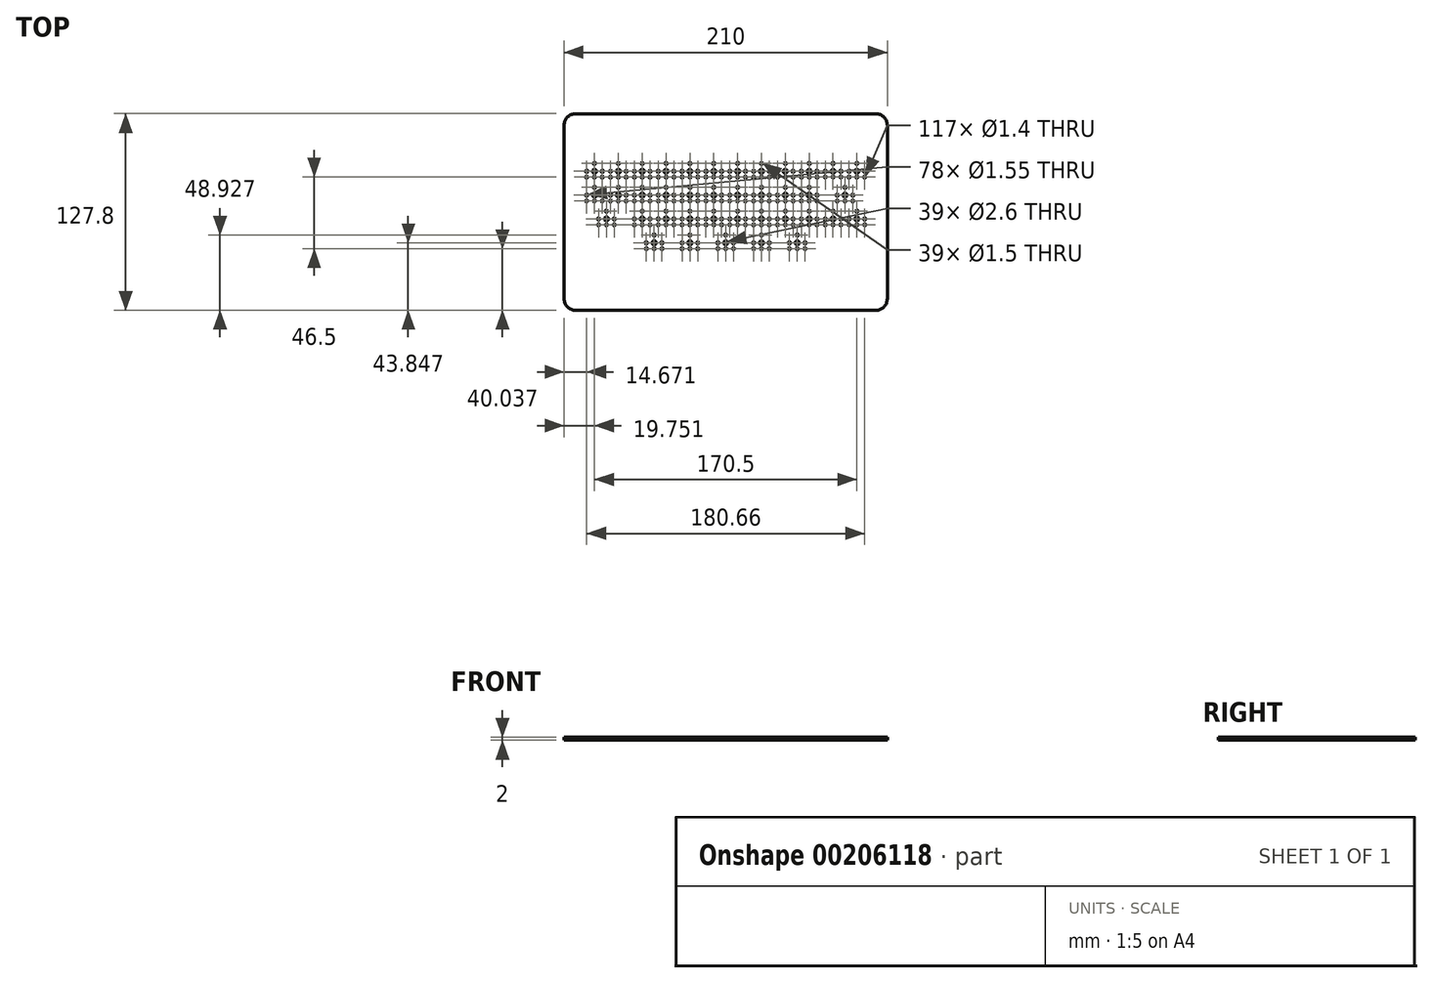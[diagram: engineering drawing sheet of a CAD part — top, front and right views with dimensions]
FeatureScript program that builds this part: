
annotation { "Feature Type Name" : "Feature", "Feature Type Description" : "" }
export const myFeature = defineFeature(function(context is Context, id is Id, definition is map)
    precondition{}
    {
        {
            var Q0;
            Q0=qCreatedBy(makeId("Top.planeOp"),FACE);
            var sketch = newSketch(context, id + "F0", { "sketchPlane" : qUnion([Q0])});
            skLineSegment(sketch, "E0", {"start": v(-79.74, 27.29) * mm, "end": v(-79.74, 14.29) * mm, "construction": true});
            skLineSegment(sketch, "E1.bottom", {"start": v(-73.74, 26.49) * mm, "end": v(-85.74, 26.49) * mm, "construction": true});
            skLineSegment(sketch, "E1.top", {"start": v(-73.74, 15.09) * mm, "end": v(-85.74, 15.09) * mm, "construction": true});
            skLineSegment(sketch, "E1.left", {"start": v(-73.74, 26.49) * mm, "end": v(-73.74, 15.09) * mm, "construction": true});
            skLineSegment(sketch, "E1.right", {"start": v(-85.74, 26.49) * mm, "end": v(-85.74, 15.09) * mm, "construction": true});
            skPoint(sketch, "E1.middle", {"position": v(-79.74, 20.79) * mm});
            skLineSegment(sketch, "E2", {"start": v(-79.74, 15.09) * mm, "end": v(-79.74, 20.09) * mm, "construction": true});
            skCircle(sketch, "E3", {"center": v(-79.74, 20.09) * mm, "radius": 1.3 * mm});
            skLineSegment(sketch, "E4", {"start": v(-79.74, 20.09) * mm, "end": v(-79.74, 17.59) * mm, "construction": true});
            skLineSegment(sketch, "E5", {"start": v(-79.74, 20.09) * mm, "end": v(-79.74, 16.28) * mm, "construction": true});
            skLineSegment(sketch, "E6", {"start": v(-79.74, 16.28) * mm, "end": v(-74.66, 16.28) * mm, "construction": true});
            skCircle(sketch, "E7", {"center": v(-74.66, 16.28) * mm, "radius": 0.7 * mm});
            skCircle(sketch, "E8", {"center": v(-79.74, 16.28) * mm, "radius": 0.7 * mm});
            skCircle(sketch, "E9.MirrorC", {"center": v(-84.82, 16.28) * mm, "radius": 0.7 * mm});
            skLineSegment(sketch, "E10", {"start": v(-79.74, 20.09) * mm, "end": v(-74.66, 20.09) * mm, "construction": true});
            skCircle(sketch, "E11", {"center": v(-74.66, 20.09) * mm, "radius": 0.78 * mm});
            skCircle(sketch, "E12.MirrorC", {"center": v(-84.82, 20.09) * mm, "radius": 0.78 * mm});
            skLineSegment(sketch, "E13", {"start": v(-79.74, 20.09) * mm, "end": v(-79.74, 25.17) * mm, "construction": true});
            skCircle(sketch, "E14", {"center": v(-79.74, 25.17) * mm, "radius": 0.75 * mm});
            skCircle(sketch, "E15.1.0.0", {"center": v(-64.24, 25.17) * mm, "radius": 0.75 * mm});
            skCircle(sketch, "E15.1.0.1", {"center": v(-69.32, 20.09) * mm, "radius": 0.78 * mm});
            skCircle(sketch, "E15.1.0.2", {"center": v(-59.16, 20.09) * mm, "radius": 0.78 * mm});
            skCircle(sketch, "E15.1.0.3", {"center": v(-59.16, 16.28) * mm, "radius": 0.7 * mm});
            skCircle(sketch, "E15.1.0.4", {"center": v(-64.24, 16.28) * mm, "radius": 0.7 * mm});
            skCircle(sketch, "E15.1.0.5", {"center": v(-69.32, 16.28) * mm, "radius": 0.7 * mm});
            skCircle(sketch, "E15.1.0.6", {"center": v(-64.24, 20.09) * mm, "radius": 1.3 * mm});
            skCircle(sketch, "E15.2.0.0", {"center": v(-48.74, 25.17) * mm, "radius": 0.75 * mm});
            skCircle(sketch, "E15.2.0.1", {"center": v(-53.82, 20.09) * mm, "radius": 0.78 * mm});
            skCircle(sketch, "E15.2.0.2", {"center": v(-43.66, 20.09) * mm, "radius": 0.78 * mm});
            skCircle(sketch, "E15.2.0.3", {"center": v(-43.66, 16.28) * mm, "radius": 0.7 * mm});
            skCircle(sketch, "E15.2.0.4", {"center": v(-48.74, 16.28) * mm, "radius": 0.7 * mm});
            skCircle(sketch, "E15.2.0.5", {"center": v(-53.82, 16.28) * mm, "radius": 0.7 * mm});
            skCircle(sketch, "E15.2.0.6", {"center": v(-48.74, 20.09) * mm, "radius": 1.3 * mm});
            skCircle(sketch, "E15.3.0.0", {"center": v(-33.24, 25.17) * mm, "radius": 0.75 * mm});
            skCircle(sketch, "E15.3.0.1", {"center": v(-38.32, 20.09) * mm, "radius": 0.78 * mm});
            skCircle(sketch, "E15.3.0.2", {"center": v(-28.16, 20.09) * mm, "radius": 0.78 * mm});
            skCircle(sketch, "E15.3.0.3", {"center": v(-28.16, 16.28) * mm, "radius": 0.7 * mm});
            skCircle(sketch, "E15.3.0.4", {"center": v(-33.24, 16.28) * mm, "radius": 0.7 * mm});
            skCircle(sketch, "E15.3.0.5", {"center": v(-38.32, 16.28) * mm, "radius": 0.7 * mm});
            skCircle(sketch, "E15.3.0.6", {"center": v(-33.24, 20.09) * mm, "radius": 1.3 * mm});
            skCircle(sketch, "E15.4.0.0", {"center": v(-17.74, 25.17) * mm, "radius": 0.75 * mm});
            skCircle(sketch, "E15.4.0.1", {"center": v(-22.82, 20.09) * mm, "radius": 0.78 * mm});
            skCircle(sketch, "E15.4.0.2", {"center": v(-12.66, 20.09) * mm, "radius": 0.78 * mm});
            skCircle(sketch, "E15.4.0.3", {"center": v(-12.66, 16.28) * mm, "radius": 0.7 * mm});
            skCircle(sketch, "E15.4.0.4", {"center": v(-17.74, 16.28) * mm, "radius": 0.7 * mm});
            skCircle(sketch, "E15.4.0.5", {"center": v(-22.82, 16.28) * mm, "radius": 0.7 * mm});
            skCircle(sketch, "E15.4.0.6", {"center": v(-17.74, 20.09) * mm, "radius": 1.3 * mm});
            skCircle(sketch, "E15.5.0.0", {"center": v(-2.24, 25.17) * mm, "radius": 0.75 * mm});
            skCircle(sketch, "E15.5.0.1", {"center": v(-7.32, 20.09) * mm, "radius": 0.78 * mm});
            skCircle(sketch, "E15.5.0.2", {"center": v(2.84, 20.09) * mm, "radius": 0.78 * mm});
            skCircle(sketch, "E15.5.0.3", {"center": v(2.84, 16.28) * mm, "radius": 0.7 * mm});
            skCircle(sketch, "E15.5.0.4", {"center": v(-2.24, 16.28) * mm, "radius": 0.7 * mm});
            skCircle(sketch, "E15.5.0.5", {"center": v(-7.32, 16.28) * mm, "radius": 0.7 * mm});
            skCircle(sketch, "E15.5.0.6", {"center": v(-2.24, 20.09) * mm, "radius": 1.3 * mm});
            skCircle(sketch, "E15.6.0.0", {"center": v(13.26, 25.17) * mm, "radius": 0.75 * mm});
            skCircle(sketch, "E15.6.0.1", {"center": v(8.18, 20.09) * mm, "radius": 0.78 * mm});
            skCircle(sketch, "E15.6.0.2", {"center": v(18.34, 20.09) * mm, "radius": 0.78 * mm});
            skCircle(sketch, "E15.6.0.3", {"center": v(18.34, 16.28) * mm, "radius": 0.7 * mm});
            skCircle(sketch, "E15.6.0.4", {"center": v(13.26, 16.28) * mm, "radius": 0.7 * mm});
            skCircle(sketch, "E15.6.0.5", {"center": v(8.18, 16.28) * mm, "radius": 0.7 * mm});
            skCircle(sketch, "E15.6.0.6", {"center": v(13.26, 20.09) * mm, "radius": 1.3 * mm});
            skCircle(sketch, "E15.7.0.0", {"center": v(28.76, 25.17) * mm, "radius": 0.75 * mm});
            skCircle(sketch, "E15.7.0.1", {"center": v(23.68, 20.09) * mm, "radius": 0.78 * mm});
            skCircle(sketch, "E15.7.0.2", {"center": v(33.84, 20.09) * mm, "radius": 0.78 * mm});
            skCircle(sketch, "E15.7.0.3", {"center": v(33.84, 16.28) * mm, "radius": 0.7 * mm});
            skCircle(sketch, "E15.7.0.4", {"center": v(28.76, 16.28) * mm, "radius": 0.7 * mm});
            skCircle(sketch, "E15.7.0.5", {"center": v(23.68, 16.28) * mm, "radius": 0.7 * mm});
            skCircle(sketch, "E15.7.0.6", {"center": v(28.76, 20.09) * mm, "radius": 1.3 * mm});
            skCircle(sketch, "E15.8.0.0", {"center": v(44.26, 25.17) * mm, "radius": 0.75 * mm});
            skCircle(sketch, "E15.8.0.1", {"center": v(39.18, 20.09) * mm, "radius": 0.78 * mm});
            skCircle(sketch, "E15.8.0.2", {"center": v(49.34, 20.09) * mm, "radius": 0.78 * mm});
            skCircle(sketch, "E15.8.0.3", {"center": v(49.34, 16.28) * mm, "radius": 0.7 * mm});
            skCircle(sketch, "E15.8.0.4", {"center": v(44.26, 16.28) * mm, "radius": 0.7 * mm});
            skCircle(sketch, "E15.8.0.5", {"center": v(39.18, 16.28) * mm, "radius": 0.7 * mm});
            skCircle(sketch, "E15.8.0.6", {"center": v(44.26, 20.09) * mm, "radius": 1.3 * mm});
            skCircle(sketch, "E15.9.0.0", {"center": v(59.76, 25.17) * mm, "radius": 0.75 * mm});
            skCircle(sketch, "E15.9.0.1", {"center": v(54.68, 20.09) * mm, "radius": 0.78 * mm});
            skCircle(sketch, "E15.9.0.2", {"center": v(64.84, 20.09) * mm, "radius": 0.78 * mm});
            skCircle(sketch, "E15.9.0.3", {"center": v(64.84, 16.28) * mm, "radius": 0.7 * mm});
            skCircle(sketch, "E15.9.0.4", {"center": v(59.76, 16.28) * mm, "radius": 0.7 * mm});
            skCircle(sketch, "E15.9.0.5", {"center": v(54.68, 16.28) * mm, "radius": 0.7 * mm});
            skCircle(sketch, "E15.9.0.6", {"center": v(59.76, 20.09) * mm, "radius": 1.3 * mm});
            skCircle(sketch, "E15.10.0.0", {"center": v(75.26, 25.17) * mm, "radius": 0.75 * mm});
            skCircle(sketch, "E15.10.0.1", {"center": v(70.18, 20.09) * mm, "radius": 0.78 * mm});
            skCircle(sketch, "E15.10.0.2", {"center": v(80.34, 20.09) * mm, "radius": 0.78 * mm});
            skCircle(sketch, "E15.10.0.3", {"center": v(80.34, 16.28) * mm, "radius": 0.7 * mm});
            skCircle(sketch, "E15.10.0.4", {"center": v(75.26, 16.28) * mm, "radius": 0.7 * mm});
            skCircle(sketch, "E15.10.0.5", {"center": v(70.18, 16.28) * mm, "radius": 0.7 * mm});
            skCircle(sketch, "E15.10.0.6", {"center": v(75.26, 20.09) * mm, "radius": 1.3 * mm});
            skCircle(sketch, "E15.11.0.0", {"center": v(90.76, 25.17) * mm, "radius": 0.75 * mm});
            skCircle(sketch, "E15.11.0.1", {"center": v(85.68, 20.09) * mm, "radius": 0.78 * mm});
            skCircle(sketch, "E15.11.0.2", {"center": v(95.84, 20.09) * mm, "radius": 0.78 * mm});
            skCircle(sketch, "E15.11.0.3", {"center": v(95.84, 16.28) * mm, "radius": 0.7 * mm});
            skCircle(sketch, "E15.11.0.4", {"center": v(90.76, 16.28) * mm, "radius": 0.7 * mm});
            skCircle(sketch, "E15.11.0.5", {"center": v(85.68, 16.28) * mm, "radius": 0.7 * mm});
            skCircle(sketch, "E15.11.0.6", {"center": v(90.76, 20.09) * mm, "radius": 1.3 * mm});
            skLineSegment(sketch, "E15.direction1", {"start": v(-79.74, 25.17) * mm, "end": v(-64.24, 25.17) * mm, "construction": true});
            skCircle(sketch, "E16.0.1.0", {"center": v(-74.66, 0.78) * mm, "radius": 0.7 * mm});
            skCircle(sketch, "E16.0.1.1", {"center": v(-79.74, 0.78) * mm, "radius": 0.7 * mm});
            skCircle(sketch, "E16.0.1.2", {"center": v(-84.82, 0.78) * mm, "radius": 0.7 * mm});
            skCircle(sketch, "E16.0.1.3", {"center": v(-84.82, 4.59) * mm, "radius": 0.78 * mm});
            skCircle(sketch, "E16.0.1.4", {"center": v(-79.74, 4.59) * mm, "radius": 1.3 * mm});
            skCircle(sketch, "E16.0.1.5", {"center": v(-74.66, 4.59) * mm, "radius": 0.78 * mm});
            skCircle(sketch, "E16.0.1.6", {"center": v(-79.74, 9.67) * mm, "radius": 0.75 * mm});
            skLineSegment(sketch, "E16.direction1", {"start": v(-74.66, 16.28) * mm, "end": v(-49.66, 16.28) * mm, "construction": true});
            skLineSegment(sketch, "E16.direction2", {"start": v(-74.66, 16.28) * mm, "end": v(-74.66, 0.78) * mm, "construction": true});
            skCircle(sketch, "E17.1.0.0", {"center": v(-64.24, 9.67) * mm, "radius": 0.75 * mm});
            skCircle(sketch, "E17.1.0.1", {"center": v(-59.16, 4.59) * mm, "radius": 0.78 * mm});
            skCircle(sketch, "E17.1.0.2", {"center": v(-64.24, 4.59) * mm, "radius": 1.3 * mm});
            skCircle(sketch, "E17.1.0.3", {"center": v(-69.32, 4.59) * mm, "radius": 0.78 * mm});
            skCircle(sketch, "E17.1.0.4", {"center": v(-64.24, 0.78) * mm, "radius": 0.7 * mm});
            skCircle(sketch, "E17.1.0.5", {"center": v(-59.16, 0.78) * mm, "radius": 0.7 * mm});
            skCircle(sketch, "E17.1.0.6", {"center": v(-69.32, 0.78) * mm, "radius": 0.7 * mm});
            skCircle(sketch, "E17.2.0.0", {"center": v(-48.74, 9.67) * mm, "radius": 0.75 * mm});
            skCircle(sketch, "E17.2.0.1", {"center": v(-43.66, 4.59) * mm, "radius": 0.78 * mm});
            skCircle(sketch, "E17.2.0.2", {"center": v(-48.74, 4.59) * mm, "radius": 1.3 * mm});
            skCircle(sketch, "E17.2.0.3", {"center": v(-53.82, 4.59) * mm, "radius": 0.78 * mm});
            skCircle(sketch, "E17.2.0.4", {"center": v(-48.74, 0.78) * mm, "radius": 0.7 * mm});
            skCircle(sketch, "E17.2.0.5", {"center": v(-43.66, 0.78) * mm, "radius": 0.7 * mm});
            skCircle(sketch, "E17.2.0.6", {"center": v(-53.82, 0.78) * mm, "radius": 0.7 * mm});
            skCircle(sketch, "E17.3.0.0", {"center": v(-33.24, 9.67) * mm, "radius": 0.75 * mm});
            skCircle(sketch, "E17.3.0.1", {"center": v(-28.16, 4.59) * mm, "radius": 0.78 * mm});
            skCircle(sketch, "E17.3.0.2", {"center": v(-33.24, 4.59) * mm, "radius": 1.3 * mm});
            skCircle(sketch, "E17.3.0.3", {"center": v(-38.32, 4.59) * mm, "radius": 0.78 * mm});
            skCircle(sketch, "E17.3.0.4", {"center": v(-33.24, 0.78) * mm, "radius": 0.7 * mm});
            skCircle(sketch, "E17.3.0.5", {"center": v(-28.16, 0.78) * mm, "radius": 0.7 * mm});
            skCircle(sketch, "E17.3.0.6", {"center": v(-38.32, 0.78) * mm, "radius": 0.7 * mm});
            skCircle(sketch, "E17.4.0.0", {"center": v(-17.74, 9.67) * mm, "radius": 0.75 * mm});
            skCircle(sketch, "E17.4.0.1", {"center": v(-12.66, 4.59) * mm, "radius": 0.78 * mm});
            skCircle(sketch, "E17.4.0.2", {"center": v(-17.74, 4.59) * mm, "radius": 1.3 * mm});
            skCircle(sketch, "E17.4.0.3", {"center": v(-22.82, 4.59) * mm, "radius": 0.78 * mm});
            skCircle(sketch, "E17.4.0.4", {"center": v(-17.74, 0.78) * mm, "radius": 0.7 * mm});
            skCircle(sketch, "E17.4.0.5", {"center": v(-12.66, 0.78) * mm, "radius": 0.7 * mm});
            skCircle(sketch, "E17.4.0.6", {"center": v(-22.82, 0.78) * mm, "radius": 0.7 * mm});
            skCircle(sketch, "E17.5.0.0", {"center": v(-2.24, 9.67) * mm, "radius": 0.75 * mm});
            skCircle(sketch, "E17.5.0.1", {"center": v(2.84, 4.59) * mm, "radius": 0.78 * mm});
            skCircle(sketch, "E17.5.0.2", {"center": v(-2.24, 4.59) * mm, "radius": 1.3 * mm});
            skCircle(sketch, "E17.5.0.3", {"center": v(-7.32, 4.59) * mm, "radius": 0.78 * mm});
            skCircle(sketch, "E17.5.0.4", {"center": v(-2.24, 0.78) * mm, "radius": 0.7 * mm});
            skCircle(sketch, "E17.5.0.5", {"center": v(2.84, 0.78) * mm, "radius": 0.7 * mm});
            skCircle(sketch, "E17.5.0.6", {"center": v(-7.32, 0.78) * mm, "radius": 0.7 * mm});
            skCircle(sketch, "E17.6.0.0", {"center": v(13.26, 9.67) * mm, "radius": 0.75 * mm});
            skCircle(sketch, "E17.6.0.1", {"center": v(18.34, 4.59) * mm, "radius": 0.78 * mm});
            skCircle(sketch, "E17.6.0.2", {"center": v(13.26, 4.59) * mm, "radius": 1.3 * mm});
            skCircle(sketch, "E17.6.0.3", {"center": v(8.18, 4.59) * mm, "radius": 0.78 * mm});
            skCircle(sketch, "E17.6.0.4", {"center": v(13.26, 0.78) * mm, "radius": 0.7 * mm});
            skCircle(sketch, "E17.6.0.5", {"center": v(18.34, 0.78) * mm, "radius": 0.7 * mm});
            skCircle(sketch, "E17.6.0.6", {"center": v(8.18, 0.78) * mm, "radius": 0.7 * mm});
            skCircle(sketch, "E17.7.0.0", {"center": v(28.76, 9.67) * mm, "radius": 0.75 * mm});
            skCircle(sketch, "E17.7.0.1", {"center": v(33.84, 4.59) * mm, "radius": 0.78 * mm});
            skCircle(sketch, "E17.7.0.2", {"center": v(28.76, 4.59) * mm, "radius": 1.3 * mm});
            skCircle(sketch, "E17.7.0.3", {"center": v(23.68, 4.59) * mm, "radius": 0.78 * mm});
            skCircle(sketch, "E17.7.0.4", {"center": v(28.76, 0.78) * mm, "radius": 0.7 * mm});
            skCircle(sketch, "E17.7.0.5", {"center": v(33.84, 0.78) * mm, "radius": 0.7 * mm});
            skCircle(sketch, "E17.7.0.6", {"center": v(23.68, 0.78) * mm, "radius": 0.7 * mm});
            skCircle(sketch, "E17.8.0.0", {"center": v(44.26, 9.67) * mm, "radius": 0.75 * mm});
            skCircle(sketch, "E17.8.0.1", {"center": v(49.34, 4.59) * mm, "radius": 0.78 * mm});
            skCircle(sketch, "E17.8.0.2", {"center": v(44.26, 4.59) * mm, "radius": 1.3 * mm});
            skCircle(sketch, "E17.8.0.3", {"center": v(39.18, 4.59) * mm, "radius": 0.78 * mm});
            skCircle(sketch, "E17.8.0.4", {"center": v(44.26, 0.78) * mm, "radius": 0.7 * mm});
            skCircle(sketch, "E17.8.0.5", {"center": v(49.34, 0.78) * mm, "radius": 0.7 * mm});
            skCircle(sketch, "E17.8.0.6", {"center": v(39.18, 0.78) * mm, "radius": 0.7 * mm});
            skCircle(sketch, "E17.9.0.0", {"center": v(59.76, 9.67) * mm, "radius": 0.75 * mm});
            skCircle(sketch, "E17.9.0.1", {"center": v(64.84, 4.59) * mm, "radius": 0.78 * mm});
            skCircle(sketch, "E17.9.0.2", {"center": v(59.76, 4.59) * mm, "radius": 1.3 * mm});
            skCircle(sketch, "E17.9.0.3", {"center": v(54.68, 4.59) * mm, "radius": 0.78 * mm});
            skCircle(sketch, "E17.9.0.4", {"center": v(59.76, 0.78) * mm, "radius": 0.7 * mm});
            skCircle(sketch, "E17.9.0.5", {"center": v(64.84, 0.78) * mm, "radius": 0.7 * mm});
            skCircle(sketch, "E17.9.0.6", {"center": v(54.68, 0.78) * mm, "radius": 0.7 * mm});
            skLineSegment(sketch, "E17.direction1", {"start": v(-79.74, 9.67) * mm, "end": v(-64.24, 9.67) * mm, "construction": true});
            skCircle(sketch, "E18.1.0.0", {"center": v(83.01, 9.67) * mm, "radius": 0.75 * mm});
            skCircle(sketch, "E18.1.0.1", {"center": v(88.1, 4.59) * mm, "radius": 0.78 * mm});
            skCircle(sketch, "E18.1.0.2", {"center": v(83.01, 4.59) * mm, "radius": 1.3 * mm});
            skCircle(sketch, "E18.1.0.3", {"center": v(77.93, 4.59) * mm, "radius": 0.78 * mm});
            skCircle(sketch, "E18.1.0.4", {"center": v(77.93, 0.78) * mm, "radius": 0.7 * mm});
            skCircle(sketch, "E18.1.0.5", {"center": v(83.01, 0.78) * mm, "radius": 0.7 * mm});
            skCircle(sketch, "E18.1.0.6", {"center": v(88.1, 0.78) * mm, "radius": 0.7 * mm});
            skLineSegment(sketch, "E18.direction1", {"start": v(59.76, 9.67) * mm, "end": v(83.01, 9.67) * mm, "construction": true});
            skCircle(sketch, "E19.0.1.0", {"center": v(90.76, -5.83) * mm, "radius": 0.75 * mm});
            skCircle(sketch, "E19.0.1.1", {"center": v(95.84, -10.91) * mm, "radius": 0.78 * mm});
            skCircle(sketch, "E19.0.1.2", {"center": v(90.76, -10.91) * mm, "radius": 1.3 * mm});
            skCircle(sketch, "E19.0.1.3", {"center": v(85.68, -10.91) * mm, "radius": 0.78 * mm});
            skCircle(sketch, "E19.0.1.4", {"center": v(85.68, -14.72) * mm, "radius": 0.7 * mm});
            skCircle(sketch, "E19.0.1.5", {"center": v(90.76, -14.72) * mm, "radius": 0.7 * mm});
            skCircle(sketch, "E19.0.1.6", {"center": v(95.84, -14.72) * mm, "radius": 0.7 * mm});
            skLineSegment(sketch, "E19.direction1", {"start": v(85.68, 16.28) * mm, "end": v(110.68, 16.28) * mm, "construction": true});
            skLineSegment(sketch, "E19.direction2", {"start": v(85.68, 16.28) * mm, "end": v(85.68, -14.72) * mm, "construction": true});
            skCircle(sketch, "E20.1.0.0", {"center": v(80.34, -14.72) * mm, "radius": 0.7 * mm});
            skCircle(sketch, "E20.1.0.1", {"center": v(75.26, -14.72) * mm, "radius": 0.7 * mm});
            skCircle(sketch, "E20.1.0.2", {"center": v(70.18, -14.72) * mm, "radius": 0.7 * mm});
            skCircle(sketch, "E20.1.0.3", {"center": v(70.18, -10.91) * mm, "radius": 0.78 * mm});
            skCircle(sketch, "E20.1.0.4", {"center": v(75.26, -10.91) * mm, "radius": 1.3 * mm});
            skCircle(sketch, "E20.1.0.5", {"center": v(80.34, -10.91) * mm, "radius": 0.78 * mm});
            skCircle(sketch, "E20.1.0.6", {"center": v(75.26, -5.83) * mm, "radius": 0.75 * mm});
            skCircle(sketch, "E20.2.0.0", {"center": v(64.84, -14.72) * mm, "radius": 0.7 * mm});
            skCircle(sketch, "E20.2.0.1", {"center": v(59.76, -14.72) * mm, "radius": 0.7 * mm});
            skCircle(sketch, "E20.2.0.2", {"center": v(54.68, -14.72) * mm, "radius": 0.7 * mm});
            skCircle(sketch, "E20.2.0.3", {"center": v(54.68, -10.91) * mm, "radius": 0.78 * mm});
            skCircle(sketch, "E20.2.0.4", {"center": v(59.76, -10.91) * mm, "radius": 1.3 * mm});
            skCircle(sketch, "E20.2.0.5", {"center": v(64.84, -10.91) * mm, "radius": 0.78 * mm});
            skCircle(sketch, "E20.2.0.6", {"center": v(59.76, -5.83) * mm, "radius": 0.75 * mm});
            skCircle(sketch, "E20.3.0.0", {"center": v(49.34, -14.72) * mm, "radius": 0.7 * mm});
            skCircle(sketch, "E20.3.0.1", {"center": v(44.26, -14.72) * mm, "radius": 0.7 * mm});
            skCircle(sketch, "E20.3.0.2", {"center": v(39.18, -14.72) * mm, "radius": 0.7 * mm});
            skCircle(sketch, "E20.3.0.3", {"center": v(39.18, -10.91) * mm, "radius": 0.78 * mm});
            skCircle(sketch, "E20.3.0.4", {"center": v(44.26, -10.91) * mm, "radius": 1.3 * mm});
            skCircle(sketch, "E20.3.0.5", {"center": v(49.34, -10.91) * mm, "radius": 0.78 * mm});
            skCircle(sketch, "E20.3.0.6", {"center": v(44.26, -5.83) * mm, "radius": 0.75 * mm});
            skCircle(sketch, "E20.4.0.0", {"center": v(33.84, -14.72) * mm, "radius": 0.7 * mm});
            skCircle(sketch, "E20.4.0.1", {"center": v(28.76, -14.72) * mm, "radius": 0.7 * mm});
            skCircle(sketch, "E20.4.0.2", {"center": v(23.68, -14.72) * mm, "radius": 0.7 * mm});
            skCircle(sketch, "E20.4.0.3", {"center": v(23.68, -10.91) * mm, "radius": 0.78 * mm});
            skCircle(sketch, "E20.4.0.4", {"center": v(28.76, -10.91) * mm, "radius": 1.3 * mm});
            skCircle(sketch, "E20.4.0.5", {"center": v(33.84, -10.91) * mm, "radius": 0.78 * mm});
            skCircle(sketch, "E20.4.0.6", {"center": v(28.76, -5.83) * mm, "radius": 0.75 * mm});
            skCircle(sketch, "E20.5.0.0", {"center": v(18.34, -14.72) * mm, "radius": 0.7 * mm});
            skCircle(sketch, "E20.5.0.1", {"center": v(13.26, -14.72) * mm, "radius": 0.7 * mm});
            skCircle(sketch, "E20.5.0.2", {"center": v(8.18, -14.72) * mm, "radius": 0.7 * mm});
            skCircle(sketch, "E20.5.0.3", {"center": v(8.18, -10.91) * mm, "radius": 0.78 * mm});
            skCircle(sketch, "E20.5.0.4", {"center": v(13.26, -10.91) * mm, "radius": 1.3 * mm});
            skCircle(sketch, "E20.5.0.5", {"center": v(18.34, -10.91) * mm, "radius": 0.78 * mm});
            skCircle(sketch, "E20.5.0.6", {"center": v(13.26, -5.83) * mm, "radius": 0.75 * mm});
            skCircle(sketch, "E20.6.0.0", {"center": v(2.84, -14.72) * mm, "radius": 0.7 * mm});
            skCircle(sketch, "E20.6.0.1", {"center": v(-2.24, -14.72) * mm, "radius": 0.7 * mm});
            skCircle(sketch, "E20.6.0.2", {"center": v(-7.32, -14.72) * mm, "radius": 0.7 * mm});
            skCircle(sketch, "E20.6.0.3", {"center": v(-7.32, -10.91) * mm, "radius": 0.78 * mm});
            skCircle(sketch, "E20.6.0.4", {"center": v(-2.24, -10.91) * mm, "radius": 1.3 * mm});
            skCircle(sketch, "E20.6.0.5", {"center": v(2.84, -10.91) * mm, "radius": 0.78 * mm});
            skCircle(sketch, "E20.6.0.6", {"center": v(-2.24, -5.83) * mm, "radius": 0.75 * mm});
            skCircle(sketch, "E20.7.0.0", {"center": v(-12.66, -14.72) * mm, "radius": 0.7 * mm});
            skCircle(sketch, "E20.7.0.1", {"center": v(-17.74, -14.72) * mm, "radius": 0.7 * mm});
            skCircle(sketch, "E20.7.0.2", {"center": v(-22.82, -14.72) * mm, "radius": 0.7 * mm});
            skCircle(sketch, "E20.7.0.3", {"center": v(-22.82, -10.91) * mm, "radius": 0.78 * mm});
            skCircle(sketch, "E20.7.0.4", {"center": v(-17.74, -10.91) * mm, "radius": 1.3 * mm});
            skCircle(sketch, "E20.7.0.5", {"center": v(-12.66, -10.91) * mm, "radius": 0.78 * mm});
            skCircle(sketch, "E20.7.0.6", {"center": v(-17.74, -5.83) * mm, "radius": 0.75 * mm});
            skCircle(sketch, "E20.8.0.0", {"center": v(-28.16, -14.72) * mm, "radius": 0.7 * mm});
            skCircle(sketch, "E20.8.0.1", {"center": v(-33.24, -14.72) * mm, "radius": 0.7 * mm});
            skCircle(sketch, "E20.8.0.2", {"center": v(-38.32, -14.72) * mm, "radius": 0.7 * mm});
            skCircle(sketch, "E20.8.0.3", {"center": v(-38.32, -10.91) * mm, "radius": 0.78 * mm});
            skCircle(sketch, "E20.8.0.4", {"center": v(-33.24, -10.91) * mm, "radius": 1.3 * mm});
            skCircle(sketch, "E20.8.0.5", {"center": v(-28.16, -10.91) * mm, "radius": 0.78 * mm});
            skCircle(sketch, "E20.8.0.6", {"center": v(-33.24, -5.83) * mm, "radius": 0.75 * mm});
            skCircle(sketch, "E20.9.0.0", {"center": v(-43.66, -14.72) * mm, "radius": 0.7 * mm});
            skCircle(sketch, "E20.9.0.1", {"center": v(-48.74, -14.72) * mm, "radius": 0.7 * mm});
            skCircle(sketch, "E20.9.0.2", {"center": v(-53.82, -14.72) * mm, "radius": 0.7 * mm});
            skCircle(sketch, "E20.9.0.3", {"center": v(-53.82, -10.91) * mm, "radius": 0.78 * mm});
            skCircle(sketch, "E20.9.0.4", {"center": v(-48.74, -10.91) * mm, "radius": 1.3 * mm});
            skCircle(sketch, "E20.9.0.5", {"center": v(-43.66, -10.91) * mm, "radius": 0.78 * mm});
            skCircle(sketch, "E20.9.0.6", {"center": v(-48.74, -5.83) * mm, "radius": 0.75 * mm});
            skLineSegment(sketch, "E20.direction1", {"start": v(85.68, -14.72) * mm, "end": v(70.18, -14.72) * mm, "construction": true});
            skCircle(sketch, "E21.1.0.0", {"center": v(-71.99, -14.72) * mm, "radius": 0.7 * mm});
            skCircle(sketch, "E21.1.0.1", {"center": v(-71.99, -10.91) * mm, "radius": 1.3 * mm});
            skCircle(sketch, "E21.1.0.2", {"center": v(-66.9, -10.91) * mm, "radius": 0.78 * mm});
            skCircle(sketch, "E21.1.0.3", {"center": v(-77.07, -14.72) * mm, "radius": 0.7 * mm});
            skCircle(sketch, "E21.1.0.4", {"center": v(-77.07, -10.91) * mm, "radius": 0.78 * mm});
            skCircle(sketch, "E21.1.0.5", {"center": v(-71.99, -5.83) * mm, "radius": 0.75 * mm});
            skLineSegment(sketch, "E21.direction1", {"start": v(-53.82, -14.72) * mm, "end": v(-77.07, -14.72) * mm, "construction": true});
            skCircle(sketch, "E22.1.0.0", {"center": v(-66.9, -14.72) * mm, "radius": 0.7 * mm});
            skLineSegment(sketch, "E22.direction1", {"start": v(-43.66, -14.72) * mm, "end": v(-66.9, -14.72) * mm, "construction": true});
            skCircle(sketch, "E23.0.1.0", {"center": v(-17.74, -21.33) * mm, "radius": 0.75 * mm});
            skCircle(sketch, "E23.0.1.1", {"center": v(-22.82, -26.41) * mm, "radius": 0.78 * mm});
            skCircle(sketch, "E23.0.1.2", {"center": v(-17.74, -26.41) * mm, "radius": 1.3 * mm});
            skCircle(sketch, "E23.0.1.3", {"center": v(-12.66, -26.41) * mm, "radius": 0.78 * mm});
            skCircle(sketch, "E23.0.1.4", {"center": v(-12.66, -30.22) * mm, "radius": 0.7 * mm});
            skCircle(sketch, "E23.0.1.5", {"center": v(-17.74, -30.22) * mm, "radius": 0.7 * mm});
            skCircle(sketch, "E23.0.1.6", {"center": v(-22.82, -30.22) * mm, "radius": 0.7 * mm});
            skLineSegment(sketch, "E23.direction1", {"start": v(-22.82, -14.72) * mm, "end": v(2.18, -14.72) * mm, "construction": true});
            skLineSegment(sketch, "E23.direction2", {"start": v(-22.82, -14.72) * mm, "end": v(-22.82, -30.22) * mm, "construction": true});
            skCircle(sketch, "E24.1.0.0", {"center": v(0.43, -26.41) * mm, "radius": 0.78 * mm});
            skCircle(sketch, "E24.1.0.1", {"center": v(5.51, -21.33) * mm, "radius": 0.75 * mm});
            skCircle(sketch, "E24.1.0.2", {"center": v(5.51, -26.41) * mm, "radius": 1.3 * mm});
            skCircle(sketch, "E24.1.0.3", {"center": v(10.6, -26.41) * mm, "radius": 0.78 * mm});
            skCircle(sketch, "E24.1.0.4", {"center": v(10.6, -30.22) * mm, "radius": 0.7 * mm});
            skCircle(sketch, "E24.1.0.5", {"center": v(5.51, -30.22) * mm, "radius": 0.7 * mm});
            skCircle(sketch, "E24.1.0.6", {"center": v(0.43, -30.22) * mm, "radius": 0.7 * mm});
            skCircle(sketch, "E24.2.0.0", {"center": v(23.68, -26.41) * mm, "radius": 0.78 * mm});
            skCircle(sketch, "E24.2.0.1", {"center": v(28.76, -21.33) * mm, "radius": 0.75 * mm});
            skCircle(sketch, "E24.2.0.2", {"center": v(28.76, -26.41) * mm, "radius": 1.3 * mm});
            skCircle(sketch, "E24.2.0.3", {"center": v(33.84, -26.41) * mm, "radius": 0.78 * mm});
            skCircle(sketch, "E24.2.0.4", {"center": v(33.84, -30.22) * mm, "radius": 0.7 * mm});
            skCircle(sketch, "E24.2.0.5", {"center": v(28.76, -30.22) * mm, "radius": 0.7 * mm});
            skCircle(sketch, "E24.2.0.6", {"center": v(23.68, -30.22) * mm, "radius": 0.7 * mm});
            skCircle(sketch, "E24.3.0.0", {"center": v(46.93, -26.41) * mm, "radius": 0.78 * mm});
            skCircle(sketch, "E24.3.0.1", {"center": v(52.01, -21.33) * mm, "radius": 0.75 * mm});
            skCircle(sketch, "E24.3.0.2", {"center": v(52.01, -26.41) * mm, "radius": 1.3 * mm});
            skCircle(sketch, "E24.3.0.3", {"center": v(57.1, -26.41) * mm, "radius": 0.78 * mm});
            skCircle(sketch, "E24.3.0.4", {"center": v(57.1, -30.22) * mm, "radius": 0.7 * mm});
            skCircle(sketch, "E24.3.0.5", {"center": v(52.01, -30.22) * mm, "radius": 0.7 * mm});
            skCircle(sketch, "E24.3.0.6", {"center": v(46.93, -30.22) * mm, "radius": 0.7 * mm});
            skLineSegment(sketch, "E24.direction1", {"start": v(-22.82, -30.22) * mm, "end": v(0.43, -30.22) * mm, "construction": true});
            skCircle(sketch, "E25.1.0.0", {"center": v(-35.9, -30.22) * mm, "radius": 0.7 * mm});
            skCircle(sketch, "E25.1.0.1", {"center": v(-40.99, -30.22) * mm, "radius": 0.7 * mm});
            skCircle(sketch, "E25.1.0.2", {"center": v(-35.9, -26.41) * mm, "radius": 0.78 * mm});
            skCircle(sketch, "E25.1.0.3", {"center": v(-46.07, -30.22) * mm, "radius": 0.7 * mm});
            skCircle(sketch, "E25.1.0.4", {"center": v(-40.99, -26.41) * mm, "radius": 1.3 * mm});
            skCircle(sketch, "E25.1.0.5", {"center": v(-46.07, -26.41) * mm, "radius": 0.78 * mm});
            skCircle(sketch, "E25.1.0.6", {"center": v(-40.99, -21.33) * mm, "radius": 0.75 * mm});
            skLineSegment(sketch, "E25.direction1", {"start": v(-22.82, -30.22) * mm, "end": v(-46.07, -30.22) * mm, "construction": true});
            skLineSegment(sketch, "E26", {"start": v(-91.99, 57.54) * mm, "end": v(103.01, 57.54) * mm});
            skLineSegment(sketch, "E27", {"start": v(110.51, 50.04) * mm, "end": v(110.51, -54.96) * mm});
            skLineSegment(sketch, "E28", {"start": v(-99.49, 50.04) * mm, "end": v(-99.49, -54.96) * mm});
            skLineSegment(sketch, "E29", {"start": v(-91.99, -62.46) * mm, "end": v(103.01, -62.46) * mm});
            skArc(sketch, "E30", {"start": v(-91.99, 57.54) * mm, "mid": v(-97.3, 55.34) * mm, "end": v(-99.49, 50.04) * mm});
            skArc(sketch, "E31", {"start": v(103.01, -62.46) * mm, "mid": v(108.31, -60.27) * mm, "end": v(110.51, -54.96) * mm});
            skArc(sketch, "E32", {"start": v(-99.49, -54.96) * mm, "mid": v(-97.3, -60.27) * mm, "end": v(-91.99, -62.46) * mm});
            skArc(sketch, "E33", {"start": v(110.51, 50.04) * mm, "mid": v(108.31, 55.34) * mm, "end": v(103.01, 57.54) * mm});
            skSolve(sketch);
        }
        {
            var Q0;
            Q0=makeQuery(id+"F0.imprint","IMPRINT",FACE,{"disambiguationData":[TD([[makeQuery(id+"F0.imprint","IMPRINT",EDGE,{"derivedFrom":sQuery(id+"F0.wireOp",EDGE,"E3")}),-1.0]])]});
            extrude(context, id + "F1", {"entities" : qUnion([Q0]), "depth" : 2 * mm});
        }
        {
            var Q0;
            Q0=makeQuery(id+"F1.opExtrude","CAP_FACE",FACE,{"disambiguationData":[OSD([sQuery(id+"F0.wireOp",EDGE,"E3"),sQuery(id+"F0.wireOp",EDGE,"E7"),sQuery(id+"F0.wireOp",EDGE,"E8"),sQuery(id+"F0.wireOp",EDGE,"E9.MirrorC"),sQuery(id+"F0.wireOp",EDGE,"E11"),sQuery(id+"F0.wireOp",EDGE,"E12.MirrorC"),sQuery(id+"F0.wireOp",EDGE,"E14"),sQuery(id+"F0.wireOp",EDGE,"E15.1.0.0"),sQuery(id+"F0.wireOp",EDGE,"E15.1.0.1"),sQuery(id+"F0.wireOp",EDGE,"E15.1.0.2"),sQuery(id+"F0.wireOp",EDGE,"E15.1.0.3"),sQuery(id+"F0.wireOp",EDGE,"E15.1.0.4"),sQuery(id+"F0.wireOp",EDGE,"E15.1.0.5"),sQuery(id+"F0.wireOp",EDGE,"E15.1.0.6"),sQuery(id+"F0.wireOp",EDGE,"E15.2.0.0"),sQuery(id+"F0.wireOp",EDGE,"E15.2.0.1"),sQuery(id+"F0.wireOp",EDGE,"E15.2.0.2"),sQuery(id+"F0.wireOp",EDGE,"E15.2.0.3"),sQuery(id+"F0.wireOp",EDGE,"E15.2.0.4"),sQuery(id+"F0.wireOp",EDGE,"E15.2.0.5"),sQuery(id+"F0.wireOp",EDGE,"E15.2.0.6"),sQuery(id+"F0.wireOp",EDGE,"E15.3.0.0"),sQuery(id+"F0.wireOp",EDGE,"E15.3.0.1"),sQuery(id+"F0.wireOp",EDGE,"E15.3.0.2"),sQuery(id+"F0.wireOp",EDGE,"E15.3.0.3"),sQuery(id+"F0.wireOp",EDGE,"E15.3.0.4"),sQuery(id+"F0.wireOp",EDGE,"E15.3.0.5"),sQuery(id+"F0.wireOp",EDGE,"E15.3.0.6"),sQuery(id+"F0.wireOp",EDGE,"E15.4.0.0"),sQuery(id+"F0.wireOp",EDGE,"E15.4.0.1"),sQuery(id+"F0.wireOp",EDGE,"E15.4.0.2"),sQuery(id+"F0.wireOp",EDGE,"E15.4.0.3"),sQuery(id+"F0.wireOp",EDGE,"E15.4.0.4"),sQuery(id+"F0.wireOp",EDGE,"E15.4.0.5"),sQuery(id+"F0.wireOp",EDGE,"E15.4.0.6"),sQuery(id+"F0.wireOp",EDGE,"E15.5.0.0"),sQuery(id+"F0.wireOp",EDGE,"E15.5.0.1"),sQuery(id+"F0.wireOp",EDGE,"E15.5.0.2"),sQuery(id+"F0.wireOp",EDGE,"E15.5.0.3"),sQuery(id+"F0.wireOp",EDGE,"E15.5.0.4"),sQuery(id+"F0.wireOp",EDGE,"E15.5.0.5"),sQuery(id+"F0.wireOp",EDGE,"E15.5.0.6"),sQuery(id+"F0.wireOp",EDGE,"E15.6.0.0"),sQuery(id+"F0.wireOp",EDGE,"E15.6.0.1"),sQuery(id+"F0.wireOp",EDGE,"E15.6.0.2"),sQuery(id+"F0.wireOp",EDGE,"E15.6.0.3"),sQuery(id+"F0.wireOp",EDGE,"E15.6.0.4"),sQuery(id+"F0.wireOp",EDGE,"E15.6.0.5"),sQuery(id+"F0.wireOp",EDGE,"E15.6.0.6"),sQuery(id+"F0.wireOp",EDGE,"E15.7.0.0"),sQuery(id+"F0.wireOp",EDGE,"E15.7.0.1"),sQuery(id+"F0.wireOp",EDGE,"E15.7.0.2"),sQuery(id+"F0.wireOp",EDGE,"E15.7.0.3"),sQuery(id+"F0.wireOp",EDGE,"E15.7.0.4"),sQuery(id+"F0.wireOp",EDGE,"E15.7.0.5"),sQuery(id+"F0.wireOp",EDGE,"E15.7.0.6"),sQuery(id+"F0.wireOp",EDGE,"E15.8.0.0"),sQuery(id+"F0.wireOp",EDGE,"E15.8.0.1"),sQuery(id+"F0.wireOp",EDGE,"E15.8.0.2"),sQuery(id+"F0.wireOp",EDGE,"E15.8.0.3"),sQuery(id+"F0.wireOp",EDGE,"E15.8.0.4"),sQuery(id+"F0.wireOp",EDGE,"E15.8.0.5"),sQuery(id+"F0.wireOp",EDGE,"E15.8.0.6"),sQuery(id+"F0.wireOp",EDGE,"E15.9.0.0"),sQuery(id+"F0.wireOp",EDGE,"E15.9.0.1"),sQuery(id+"F0.wireOp",EDGE,"E15.9.0.2"),sQuery(id+"F0.wireOp",EDGE,"E15.9.0.3"),sQuery(id+"F0.wireOp",EDGE,"E15.9.0.4"),sQuery(id+"F0.wireOp",EDGE,"E15.9.0.5"),sQuery(id+"F0.wireOp",EDGE,"E15.9.0.6"),sQuery(id+"F0.wireOp",EDGE,"E15.10.0.0"),sQuery(id+"F0.wireOp",EDGE,"E15.10.0.1"),sQuery(id+"F0.wireOp",EDGE,"E15.10.0.2"),sQuery(id+"F0.wireOp",EDGE,"E15.10.0.3"),sQuery(id+"F0.wireOp",EDGE,"E15.10.0.4"),sQuery(id+"F0.wireOp",EDGE,"E15.10.0.5"),sQuery(id+"F0.wireOp",EDGE,"E15.10.0.6"),sQuery(id+"F0.wireOp",EDGE,"E15.11.0.0"),sQuery(id+"F0.wireOp",EDGE,"E15.11.0.1"),sQuery(id+"F0.wireOp",EDGE,"E15.11.0.2"),sQuery(id+"F0.wireOp",EDGE,"E15.11.0.3"),sQuery(id+"F0.wireOp",EDGE,"E15.11.0.4"),sQuery(id+"F0.wireOp",EDGE,"E15.11.0.5"),sQuery(id+"F0.wireOp",EDGE,"E15.11.0.6"),sQuery(id+"F0.wireOp",EDGE,"E16.0.1.0"),sQuery(id+"F0.wireOp",EDGE,"E16.0.1.1"),sQuery(id+"F0.wireOp",EDGE,"E16.0.1.2"),sQuery(id+"F0.wireOp",EDGE,"E16.0.1.3"),sQuery(id+"F0.wireOp",EDGE,"E16.0.1.4"),sQuery(id+"F0.wireOp",EDGE,"E16.0.1.5"),sQuery(id+"F0.wireOp",EDGE,"E16.0.1.6"),sQuery(id+"F0.wireOp",EDGE,"E17.1.0.0"),sQuery(id+"F0.wireOp",EDGE,"E17.1.0.1"),sQuery(id+"F0.wireOp",EDGE,"E17.1.0.2"),sQuery(id+"F0.wireOp",EDGE,"E17.1.0.3"),sQuery(id+"F0.wireOp",EDGE,"E17.1.0.4"),sQuery(id+"F0.wireOp",EDGE,"E17.1.0.5"),sQuery(id+"F0.wireOp",EDGE,"E17.1.0.6"),sQuery(id+"F0.wireOp",EDGE,"E17.2.0.0"),sQuery(id+"F0.wireOp",EDGE,"E17.2.0.1"),sQuery(id+"F0.wireOp",EDGE,"E17.2.0.2"),sQuery(id+"F0.wireOp",EDGE,"E17.2.0.3"),sQuery(id+"F0.wireOp",EDGE,"E17.2.0.4"),sQuery(id+"F0.wireOp",EDGE,"E17.2.0.5"),sQuery(id+"F0.wireOp",EDGE,"E17.2.0.6"),sQuery(id+"F0.wireOp",EDGE,"E17.3.0.0"),sQuery(id+"F0.wireOp",EDGE,"E17.3.0.1"),sQuery(id+"F0.wireOp",EDGE,"E17.3.0.2"),sQuery(id+"F0.wireOp",EDGE,"E17.3.0.3"),sQuery(id+"F0.wireOp",EDGE,"E17.3.0.4"),sQuery(id+"F0.wireOp",EDGE,"E17.3.0.5"),sQuery(id+"F0.wireOp",EDGE,"E17.3.0.6"),sQuery(id+"F0.wireOp",EDGE,"E17.4.0.0"),sQuery(id+"F0.wireOp",EDGE,"E17.4.0.1"),sQuery(id+"F0.wireOp",EDGE,"E17.4.0.2"),sQuery(id+"F0.wireOp",EDGE,"E17.4.0.3"),sQuery(id+"F0.wireOp",EDGE,"E17.4.0.4"),sQuery(id+"F0.wireOp",EDGE,"E17.4.0.5"),sQuery(id+"F0.wireOp",EDGE,"E17.4.0.6"),sQuery(id+"F0.wireOp",EDGE,"E17.5.0.0"),sQuery(id+"F0.wireOp",EDGE,"E17.5.0.1"),sQuery(id+"F0.wireOp",EDGE,"E17.5.0.2"),sQuery(id+"F0.wireOp",EDGE,"E17.5.0.3"),sQuery(id+"F0.wireOp",EDGE,"E17.5.0.4"),sQuery(id+"F0.wireOp",EDGE,"E17.5.0.5"),sQuery(id+"F0.wireOp",EDGE,"E17.5.0.6"),sQuery(id+"F0.wireOp",EDGE,"E17.6.0.0"),sQuery(id+"F0.wireOp",EDGE,"E17.6.0.1"),sQuery(id+"F0.wireOp",EDGE,"E17.6.0.2"),sQuery(id+"F0.wireOp",EDGE,"E17.6.0.3"),sQuery(id+"F0.wireOp",EDGE,"E17.6.0.4"),sQuery(id+"F0.wireOp",EDGE,"E17.6.0.5"),sQuery(id+"F0.wireOp",EDGE,"E17.6.0.6"),sQuery(id+"F0.wireOp",EDGE,"E17.7.0.0"),sQuery(id+"F0.wireOp",EDGE,"E17.7.0.1"),sQuery(id+"F0.wireOp",EDGE,"E17.7.0.2"),sQuery(id+"F0.wireOp",EDGE,"E17.7.0.3"),sQuery(id+"F0.wireOp",EDGE,"E17.7.0.4"),sQuery(id+"F0.wireOp",EDGE,"E17.7.0.5"),sQuery(id+"F0.wireOp",EDGE,"E17.7.0.6"),sQuery(id+"F0.wireOp",EDGE,"E17.8.0.0"),sQuery(id+"F0.wireOp",EDGE,"E17.8.0.1"),sQuery(id+"F0.wireOp",EDGE,"E17.8.0.2"),sQuery(id+"F0.wireOp",EDGE,"E17.8.0.3"),sQuery(id+"F0.wireOp",EDGE,"E17.8.0.4"),sQuery(id+"F0.wireOp",EDGE,"E17.8.0.5"),sQuery(id+"F0.wireOp",EDGE,"E17.8.0.6"),sQuery(id+"F0.wireOp",EDGE,"E17.9.0.0"),sQuery(id+"F0.wireOp",EDGE,"E17.9.0.1"),sQuery(id+"F0.wireOp",EDGE,"E17.9.0.2"),sQuery(id+"F0.wireOp",EDGE,"E17.9.0.3"),sQuery(id+"F0.wireOp",EDGE,"E17.9.0.4"),sQuery(id+"F0.wireOp",EDGE,"E17.9.0.5"),sQuery(id+"F0.wireOp",EDGE,"E17.9.0.6"),sQuery(id+"F0.wireOp",EDGE,"E18.1.0.0"),sQuery(id+"F0.wireOp",EDGE,"E18.1.0.1"),sQuery(id+"F0.wireOp",EDGE,"E18.1.0.2"),sQuery(id+"F0.wireOp",EDGE,"E18.1.0.3"),sQuery(id+"F0.wireOp",EDGE,"E18.1.0.4"),sQuery(id+"F0.wireOp",EDGE,"E18.1.0.5"),sQuery(id+"F0.wireOp",EDGE,"E18.1.0.6"),sQuery(id+"F0.wireOp",EDGE,"E19.0.1.0"),sQuery(id+"F0.wireOp",EDGE,"E19.0.1.1"),sQuery(id+"F0.wireOp",EDGE,"E19.0.1.2"),sQuery(id+"F0.wireOp",EDGE,"E19.0.1.3"),sQuery(id+"F0.wireOp",EDGE,"E19.0.1.4"),sQuery(id+"F0.wireOp",EDGE,"E19.0.1.5"),sQuery(id+"F0.wireOp",EDGE,"E19.0.1.6"),sQuery(id+"F0.wireOp",EDGE,"E20.1.0.0"),sQuery(id+"F0.wireOp",EDGE,"E20.1.0.1"),sQuery(id+"F0.wireOp",EDGE,"E20.1.0.2"),sQuery(id+"F0.wireOp",EDGE,"E20.1.0.3"),sQuery(id+"F0.wireOp",EDGE,"E20.1.0.4"),sQuery(id+"F0.wireOp",EDGE,"E20.1.0.5"),sQuery(id+"F0.wireOp",EDGE,"E20.1.0.6"),sQuery(id+"F0.wireOp",EDGE,"E20.2.0.0"),sQuery(id+"F0.wireOp",EDGE,"E20.2.0.1"),sQuery(id+"F0.wireOp",EDGE,"E20.2.0.2"),sQuery(id+"F0.wireOp",EDGE,"E20.2.0.3"),sQuery(id+"F0.wireOp",EDGE,"E20.2.0.4"),sQuery(id+"F0.wireOp",EDGE,"E20.2.0.5"),sQuery(id+"F0.wireOp",EDGE,"E20.2.0.6"),sQuery(id+"F0.wireOp",EDGE,"E20.3.0.0"),sQuery(id+"F0.wireOp",EDGE,"E20.3.0.1"),sQuery(id+"F0.wireOp",EDGE,"E20.3.0.2"),sQuery(id+"F0.wireOp",EDGE,"E20.3.0.3"),sQuery(id+"F0.wireOp",EDGE,"E20.3.0.4"),sQuery(id+"F0.wireOp",EDGE,"E20.3.0.5"),sQuery(id+"F0.wireOp",EDGE,"E20.3.0.6"),sQuery(id+"F0.wireOp",EDGE,"E20.4.0.0"),sQuery(id+"F0.wireOp",EDGE,"E20.4.0.1"),sQuery(id+"F0.wireOp",EDGE,"E20.4.0.2"),sQuery(id+"F0.wireOp",EDGE,"E20.4.0.3"),sQuery(id+"F0.wireOp",EDGE,"E20.4.0.4"),sQuery(id+"F0.wireOp",EDGE,"E20.4.0.5"),sQuery(id+"F0.wireOp",EDGE,"E20.4.0.6"),sQuery(id+"F0.wireOp",EDGE,"E20.5.0.0"),sQuery(id+"F0.wireOp",EDGE,"E20.5.0.1"),sQuery(id+"F0.wireOp",EDGE,"E20.5.0.2"),sQuery(id+"F0.wireOp",EDGE,"E20.5.0.3"),sQuery(id+"F0.wireOp",EDGE,"E20.5.0.4"),sQuery(id+"F0.wireOp",EDGE,"E20.5.0.5"),sQuery(id+"F0.wireOp",EDGE,"E20.5.0.6"),sQuery(id+"F0.wireOp",EDGE,"E20.6.0.0"),sQuery(id+"F0.wireOp",EDGE,"E20.6.0.1"),sQuery(id+"F0.wireOp",EDGE,"E20.6.0.2"),sQuery(id+"F0.wireOp",EDGE,"E20.6.0.3"),sQuery(id+"F0.wireOp",EDGE,"E20.6.0.4"),sQuery(id+"F0.wireOp",EDGE,"E20.6.0.5"),sQuery(id+"F0.wireOp",EDGE,"E20.6.0.6"),sQuery(id+"F0.wireOp",EDGE,"E20.7.0.0"),sQuery(id+"F0.wireOp",EDGE,"E20.7.0.1"),sQuery(id+"F0.wireOp",EDGE,"E20.7.0.2"),sQuery(id+"F0.wireOp",EDGE,"E20.7.0.3"),sQuery(id+"F0.wireOp",EDGE,"E20.7.0.4"),sQuery(id+"F0.wireOp",EDGE,"E20.7.0.5"),sQuery(id+"F0.wireOp",EDGE,"E20.7.0.6"),sQuery(id+"F0.wireOp",EDGE,"E20.8.0.0"),sQuery(id+"F0.wireOp",EDGE,"E20.8.0.1"),sQuery(id+"F0.wireOp",EDGE,"E20.8.0.2"),sQuery(id+"F0.wireOp",EDGE,"E20.8.0.3"),sQuery(id+"F0.wireOp",EDGE,"E20.8.0.4"),sQuery(id+"F0.wireOp",EDGE,"E20.8.0.5"),sQuery(id+"F0.wireOp",EDGE,"E20.8.0.6"),sQuery(id+"F0.wireOp",EDGE,"E20.9.0.0"),sQuery(id+"F0.wireOp",EDGE,"E20.9.0.1"),sQuery(id+"F0.wireOp",EDGE,"E20.9.0.2"),sQuery(id+"F0.wireOp",EDGE,"E20.9.0.3"),sQuery(id+"F0.wireOp",EDGE,"E20.9.0.4"),sQuery(id+"F0.wireOp",EDGE,"E20.9.0.5"),sQuery(id+"F0.wireOp",EDGE,"E20.9.0.6"),sQuery(id+"F0.wireOp",EDGE,"E21.1.0.0"),sQuery(id+"F0.wireOp",EDGE,"E21.1.0.1"),sQuery(id+"F0.wireOp",EDGE,"E21.1.0.2"),sQuery(id+"F0.wireOp",EDGE,"E21.1.0.3"),sQuery(id+"F0.wireOp",EDGE,"E21.1.0.4"),sQuery(id+"F0.wireOp",EDGE,"E21.1.0.5"),sQuery(id+"F0.wireOp",EDGE,"E22.1.0.0"),sQuery(id+"F0.wireOp",EDGE,"E23.0.1.0"),sQuery(id+"F0.wireOp",EDGE,"E23.0.1.1"),sQuery(id+"F0.wireOp",EDGE,"E23.0.1.2"),sQuery(id+"F0.wireOp",EDGE,"E23.0.1.3"),sQuery(id+"F0.wireOp",EDGE,"E23.0.1.4"),sQuery(id+"F0.wireOp",EDGE,"E23.0.1.5"),sQuery(id+"F0.wireOp",EDGE,"E23.0.1.6"),sQuery(id+"F0.wireOp",EDGE,"E24.1.0.0"),sQuery(id+"F0.wireOp",EDGE,"E24.1.0.1"),sQuery(id+"F0.wireOp",EDGE,"E24.1.0.2"),sQuery(id+"F0.wireOp",EDGE,"E24.1.0.3"),sQuery(id+"F0.wireOp",EDGE,"E24.1.0.4"),sQuery(id+"F0.wireOp",EDGE,"E24.1.0.5"),sQuery(id+"F0.wireOp",EDGE,"E24.1.0.6"),sQuery(id+"F0.wireOp",EDGE,"E24.2.0.0"),sQuery(id+"F0.wireOp",EDGE,"E24.2.0.1"),sQuery(id+"F0.wireOp",EDGE,"E24.2.0.2"),sQuery(id+"F0.wireOp",EDGE,"E24.2.0.3"),sQuery(id+"F0.wireOp",EDGE,"E24.2.0.4"),sQuery(id+"F0.wireOp",EDGE,"E24.2.0.5"),sQuery(id+"F0.wireOp",EDGE,"E24.2.0.6"),sQuery(id+"F0.wireOp",EDGE,"E24.3.0.0"),sQuery(id+"F0.wireOp",EDGE,"E24.3.0.1"),sQuery(id+"F0.wireOp",EDGE,"E24.3.0.2"),sQuery(id+"F0.wireOp",EDGE,"E24.3.0.3"),sQuery(id+"F0.wireOp",EDGE,"E24.3.0.4"),sQuery(id+"F0.wireOp",EDGE,"E24.3.0.5"),sQuery(id+"F0.wireOp",EDGE,"E24.3.0.6"),sQuery(id+"F0.wireOp",EDGE,"E25.1.0.0"),sQuery(id+"F0.wireOp",EDGE,"E25.1.0.1"),sQuery(id+"F0.wireOp",EDGE,"E25.1.0.2"),sQuery(id+"F0.wireOp",EDGE,"E25.1.0.3"),sQuery(id+"F0.wireOp",EDGE,"E25.1.0.4"),sQuery(id+"F0.wireOp",EDGE,"E25.1.0.5"),sQuery(id+"F0.wireOp",EDGE,"E25.1.0.6"),sQuery(id+"F0.wireOp",EDGE,"E26"),sQuery(id+"F0.wireOp",EDGE,"E27"),sQuery(id+"F0.wireOp",EDGE,"E28"),sQuery(id+"F0.wireOp",EDGE,"E29"),sQuery(id+"F0.wireOp",EDGE,"E30"),sQuery(id+"F0.wireOp",EDGE,"E31"),sQuery(id+"F0.wireOp",EDGE,"E32"),sQuery(id+"F0.wireOp",EDGE,"E33")])],"isStart":false});
            var sketch = newSketch(context, id + "F2", { "sketchPlane" : qUnion([Q0])});
            skLineSegment(sketch, "E34", {"start": v(-99.49, -54.96) * mm, "end": v(-99.49, -62.76) * mm});
            skLineSegment(sketch, "E35", {"start": v(-99.49, -54.96) * mm, "end": v(110.51, -54.96) * mm});
            skLineSegment(sketch, "E36", {"start": v(110.51, -54.96) * mm, "end": v(110.51, -62.76) * mm});
            skLineSegment(sketch, "E37", {"start": v(103.01, -70.26) * mm, "end": v(-91.99, -70.26) * mm});
            skPoint(sketch, "E38.visualSharp", {"position": v(-99.49, -70.26) * mm});
            skArc(sketch, "E38.filletArc", {"start": v(-99.49, -62.76) * mm, "mid": v(-97.3, -68.07) * mm, "end": v(-91.99, -70.26) * mm});
            skPoint(sketch, "E39.visualSharp", {"position": v(110.51, -70.26) * mm});
            skArc(sketch, "E39.filletArc", {"start": v(103.01, -70.26) * mm, "mid": v(108.31, -68.07) * mm, "end": v(110.51, -62.76) * mm});
            skSolve(sketch);
        }
        {
            var Q0;
            Q0=makeQuery(id+"F2.imprint","IMPRINT",FACE,{"disambiguationData":[TD([[makeQuery(id+"F2.imprint","IMPRINT",EDGE,{"derivedFrom":sQuery(id+"F2.wireOp",EDGE,"E35")}),-1.0]])]});
            var Q1;
            Q1=makeQuery(id+"F2.imprint","IMPRINT",FACE,{"disambiguationData":[TD([[makeQuery(id+"F2.imprint","IMPRINT",EDGE,{"derivedFrom":sQuery(id+"F2.wireOp",EDGE,"E34")}),1.0]])]});
            var Q2;
            Q2=makeQuery(id+"F1.opExtrude","CAP_FACE",FACE,{"disambiguationData":[OSD([sQuery(id+"F0.wireOp",EDGE,"E3"),sQuery(id+"F0.wireOp",EDGE,"E7"),sQuery(id+"F0.wireOp",EDGE,"E8"),sQuery(id+"F0.wireOp",EDGE,"E9.MirrorC"),sQuery(id+"F0.wireOp",EDGE,"E11"),sQuery(id+"F0.wireOp",EDGE,"E12.MirrorC"),sQuery(id+"F0.wireOp",EDGE,"E14"),sQuery(id+"F0.wireOp",EDGE,"E15.1.0.0"),sQuery(id+"F0.wireOp",EDGE,"E15.1.0.1"),sQuery(id+"F0.wireOp",EDGE,"E15.1.0.2"),sQuery(id+"F0.wireOp",EDGE,"E15.1.0.3"),sQuery(id+"F0.wireOp",EDGE,"E15.1.0.4"),sQuery(id+"F0.wireOp",EDGE,"E15.1.0.5"),sQuery(id+"F0.wireOp",EDGE,"E15.1.0.6"),sQuery(id+"F0.wireOp",EDGE,"E15.2.0.0"),sQuery(id+"F0.wireOp",EDGE,"E15.2.0.1"),sQuery(id+"F0.wireOp",EDGE,"E15.2.0.2"),sQuery(id+"F0.wireOp",EDGE,"E15.2.0.3"),sQuery(id+"F0.wireOp",EDGE,"E15.2.0.4"),sQuery(id+"F0.wireOp",EDGE,"E15.2.0.5"),sQuery(id+"F0.wireOp",EDGE,"E15.2.0.6"),sQuery(id+"F0.wireOp",EDGE,"E15.3.0.0"),sQuery(id+"F0.wireOp",EDGE,"E15.3.0.1"),sQuery(id+"F0.wireOp",EDGE,"E15.3.0.2"),sQuery(id+"F0.wireOp",EDGE,"E15.3.0.3"),sQuery(id+"F0.wireOp",EDGE,"E15.3.0.4"),sQuery(id+"F0.wireOp",EDGE,"E15.3.0.5"),sQuery(id+"F0.wireOp",EDGE,"E15.3.0.6"),sQuery(id+"F0.wireOp",EDGE,"E15.4.0.0"),sQuery(id+"F0.wireOp",EDGE,"E15.4.0.1"),sQuery(id+"F0.wireOp",EDGE,"E15.4.0.2"),sQuery(id+"F0.wireOp",EDGE,"E15.4.0.3"),sQuery(id+"F0.wireOp",EDGE,"E15.4.0.4"),sQuery(id+"F0.wireOp",EDGE,"E15.4.0.5"),sQuery(id+"F0.wireOp",EDGE,"E15.4.0.6"),sQuery(id+"F0.wireOp",EDGE,"E15.5.0.0"),sQuery(id+"F0.wireOp",EDGE,"E15.5.0.1"),sQuery(id+"F0.wireOp",EDGE,"E15.5.0.2"),sQuery(id+"F0.wireOp",EDGE,"E15.5.0.3"),sQuery(id+"F0.wireOp",EDGE,"E15.5.0.4"),sQuery(id+"F0.wireOp",EDGE,"E15.5.0.5"),sQuery(id+"F0.wireOp",EDGE,"E15.5.0.6"),sQuery(id+"F0.wireOp",EDGE,"E15.6.0.0"),sQuery(id+"F0.wireOp",EDGE,"E15.6.0.1"),sQuery(id+"F0.wireOp",EDGE,"E15.6.0.2"),sQuery(id+"F0.wireOp",EDGE,"E15.6.0.3"),sQuery(id+"F0.wireOp",EDGE,"E15.6.0.4"),sQuery(id+"F0.wireOp",EDGE,"E15.6.0.5"),sQuery(id+"F0.wireOp",EDGE,"E15.6.0.6"),sQuery(id+"F0.wireOp",EDGE,"E15.7.0.0"),sQuery(id+"F0.wireOp",EDGE,"E15.7.0.1"),sQuery(id+"F0.wireOp",EDGE,"E15.7.0.2"),sQuery(id+"F0.wireOp",EDGE,"E15.7.0.3"),sQuery(id+"F0.wireOp",EDGE,"E15.7.0.4"),sQuery(id+"F0.wireOp",EDGE,"E15.7.0.5"),sQuery(id+"F0.wireOp",EDGE,"E15.7.0.6"),sQuery(id+"F0.wireOp",EDGE,"E15.8.0.0"),sQuery(id+"F0.wireOp",EDGE,"E15.8.0.1"),sQuery(id+"F0.wireOp",EDGE,"E15.8.0.2"),sQuery(id+"F0.wireOp",EDGE,"E15.8.0.3"),sQuery(id+"F0.wireOp",EDGE,"E15.8.0.4"),sQuery(id+"F0.wireOp",EDGE,"E15.8.0.5"),sQuery(id+"F0.wireOp",EDGE,"E15.8.0.6"),sQuery(id+"F0.wireOp",EDGE,"E15.9.0.0"),sQuery(id+"F0.wireOp",EDGE,"E15.9.0.1"),sQuery(id+"F0.wireOp",EDGE,"E15.9.0.2"),sQuery(id+"F0.wireOp",EDGE,"E15.9.0.3"),sQuery(id+"F0.wireOp",EDGE,"E15.9.0.4"),sQuery(id+"F0.wireOp",EDGE,"E15.9.0.5"),sQuery(id+"F0.wireOp",EDGE,"E15.9.0.6"),sQuery(id+"F0.wireOp",EDGE,"E15.10.0.0"),sQuery(id+"F0.wireOp",EDGE,"E15.10.0.1"),sQuery(id+"F0.wireOp",EDGE,"E15.10.0.2"),sQuery(id+"F0.wireOp",EDGE,"E15.10.0.3"),sQuery(id+"F0.wireOp",EDGE,"E15.10.0.4"),sQuery(id+"F0.wireOp",EDGE,"E15.10.0.5"),sQuery(id+"F0.wireOp",EDGE,"E15.10.0.6"),sQuery(id+"F0.wireOp",EDGE,"E15.11.0.0"),sQuery(id+"F0.wireOp",EDGE,"E15.11.0.1"),sQuery(id+"F0.wireOp",EDGE,"E15.11.0.2"),sQuery(id+"F0.wireOp",EDGE,"E15.11.0.3"),sQuery(id+"F0.wireOp",EDGE,"E15.11.0.4"),sQuery(id+"F0.wireOp",EDGE,"E15.11.0.5"),sQuery(id+"F0.wireOp",EDGE,"E15.11.0.6"),sQuery(id+"F0.wireOp",EDGE,"E16.0.1.0"),sQuery(id+"F0.wireOp",EDGE,"E16.0.1.1"),sQuery(id+"F0.wireOp",EDGE,"E16.0.1.2"),sQuery(id+"F0.wireOp",EDGE,"E16.0.1.3"),sQuery(id+"F0.wireOp",EDGE,"E16.0.1.4"),sQuery(id+"F0.wireOp",EDGE,"E16.0.1.5"),sQuery(id+"F0.wireOp",EDGE,"E16.0.1.6"),sQuery(id+"F0.wireOp",EDGE,"E17.1.0.0"),sQuery(id+"F0.wireOp",EDGE,"E17.1.0.1"),sQuery(id+"F0.wireOp",EDGE,"E17.1.0.2"),sQuery(id+"F0.wireOp",EDGE,"E17.1.0.3"),sQuery(id+"F0.wireOp",EDGE,"E17.1.0.4"),sQuery(id+"F0.wireOp",EDGE,"E17.1.0.5"),sQuery(id+"F0.wireOp",EDGE,"E17.1.0.6"),sQuery(id+"F0.wireOp",EDGE,"E17.2.0.0"),sQuery(id+"F0.wireOp",EDGE,"E17.2.0.1"),sQuery(id+"F0.wireOp",EDGE,"E17.2.0.2"),sQuery(id+"F0.wireOp",EDGE,"E17.2.0.3"),sQuery(id+"F0.wireOp",EDGE,"E17.2.0.4"),sQuery(id+"F0.wireOp",EDGE,"E17.2.0.5"),sQuery(id+"F0.wireOp",EDGE,"E17.2.0.6"),sQuery(id+"F0.wireOp",EDGE,"E17.3.0.0"),sQuery(id+"F0.wireOp",EDGE,"E17.3.0.1"),sQuery(id+"F0.wireOp",EDGE,"E17.3.0.2"),sQuery(id+"F0.wireOp",EDGE,"E17.3.0.3"),sQuery(id+"F0.wireOp",EDGE,"E17.3.0.4"),sQuery(id+"F0.wireOp",EDGE,"E17.3.0.5"),sQuery(id+"F0.wireOp",EDGE,"E17.3.0.6"),sQuery(id+"F0.wireOp",EDGE,"E17.4.0.0"),sQuery(id+"F0.wireOp",EDGE,"E17.4.0.1"),sQuery(id+"F0.wireOp",EDGE,"E17.4.0.2"),sQuery(id+"F0.wireOp",EDGE,"E17.4.0.3"),sQuery(id+"F0.wireOp",EDGE,"E17.4.0.4"),sQuery(id+"F0.wireOp",EDGE,"E17.4.0.5"),sQuery(id+"F0.wireOp",EDGE,"E17.4.0.6"),sQuery(id+"F0.wireOp",EDGE,"E17.5.0.0"),sQuery(id+"F0.wireOp",EDGE,"E17.5.0.1"),sQuery(id+"F0.wireOp",EDGE,"E17.5.0.2"),sQuery(id+"F0.wireOp",EDGE,"E17.5.0.3"),sQuery(id+"F0.wireOp",EDGE,"E17.5.0.4"),sQuery(id+"F0.wireOp",EDGE,"E17.5.0.5"),sQuery(id+"F0.wireOp",EDGE,"E17.5.0.6"),sQuery(id+"F0.wireOp",EDGE,"E17.6.0.0"),sQuery(id+"F0.wireOp",EDGE,"E17.6.0.1"),sQuery(id+"F0.wireOp",EDGE,"E17.6.0.2"),sQuery(id+"F0.wireOp",EDGE,"E17.6.0.3"),sQuery(id+"F0.wireOp",EDGE,"E17.6.0.4"),sQuery(id+"F0.wireOp",EDGE,"E17.6.0.5"),sQuery(id+"F0.wireOp",EDGE,"E17.6.0.6"),sQuery(id+"F0.wireOp",EDGE,"E17.7.0.0"),sQuery(id+"F0.wireOp",EDGE,"E17.7.0.1"),sQuery(id+"F0.wireOp",EDGE,"E17.7.0.2"),sQuery(id+"F0.wireOp",EDGE,"E17.7.0.3"),sQuery(id+"F0.wireOp",EDGE,"E17.7.0.4"),sQuery(id+"F0.wireOp",EDGE,"E17.7.0.5"),sQuery(id+"F0.wireOp",EDGE,"E17.7.0.6"),sQuery(id+"F0.wireOp",EDGE,"E17.8.0.0"),sQuery(id+"F0.wireOp",EDGE,"E17.8.0.1"),sQuery(id+"F0.wireOp",EDGE,"E17.8.0.2"),sQuery(id+"F0.wireOp",EDGE,"E17.8.0.3"),sQuery(id+"F0.wireOp",EDGE,"E17.8.0.4"),sQuery(id+"F0.wireOp",EDGE,"E17.8.0.5"),sQuery(id+"F0.wireOp",EDGE,"E17.8.0.6"),sQuery(id+"F0.wireOp",EDGE,"E17.9.0.0"),sQuery(id+"F0.wireOp",EDGE,"E17.9.0.1"),sQuery(id+"F0.wireOp",EDGE,"E17.9.0.2"),sQuery(id+"F0.wireOp",EDGE,"E17.9.0.3"),sQuery(id+"F0.wireOp",EDGE,"E17.9.0.4"),sQuery(id+"F0.wireOp",EDGE,"E17.9.0.5"),sQuery(id+"F0.wireOp",EDGE,"E17.9.0.6"),sQuery(id+"F0.wireOp",EDGE,"E18.1.0.0"),sQuery(id+"F0.wireOp",EDGE,"E18.1.0.1"),sQuery(id+"F0.wireOp",EDGE,"E18.1.0.2"),sQuery(id+"F0.wireOp",EDGE,"E18.1.0.3"),sQuery(id+"F0.wireOp",EDGE,"E18.1.0.4"),sQuery(id+"F0.wireOp",EDGE,"E18.1.0.5"),sQuery(id+"F0.wireOp",EDGE,"E18.1.0.6"),sQuery(id+"F0.wireOp",EDGE,"E19.0.1.0"),sQuery(id+"F0.wireOp",EDGE,"E19.0.1.1"),sQuery(id+"F0.wireOp",EDGE,"E19.0.1.2"),sQuery(id+"F0.wireOp",EDGE,"E19.0.1.3"),sQuery(id+"F0.wireOp",EDGE,"E19.0.1.4"),sQuery(id+"F0.wireOp",EDGE,"E19.0.1.5"),sQuery(id+"F0.wireOp",EDGE,"E19.0.1.6"),sQuery(id+"F0.wireOp",EDGE,"E20.1.0.0"),sQuery(id+"F0.wireOp",EDGE,"E20.1.0.1"),sQuery(id+"F0.wireOp",EDGE,"E20.1.0.2"),sQuery(id+"F0.wireOp",EDGE,"E20.1.0.3"),sQuery(id+"F0.wireOp",EDGE,"E20.1.0.4"),sQuery(id+"F0.wireOp",EDGE,"E20.1.0.5"),sQuery(id+"F0.wireOp",EDGE,"E20.1.0.6"),sQuery(id+"F0.wireOp",EDGE,"E20.2.0.0"),sQuery(id+"F0.wireOp",EDGE,"E20.2.0.1"),sQuery(id+"F0.wireOp",EDGE,"E20.2.0.2"),sQuery(id+"F0.wireOp",EDGE,"E20.2.0.3"),sQuery(id+"F0.wireOp",EDGE,"E20.2.0.4"),sQuery(id+"F0.wireOp",EDGE,"E20.2.0.5"),sQuery(id+"F0.wireOp",EDGE,"E20.2.0.6"),sQuery(id+"F0.wireOp",EDGE,"E20.3.0.0"),sQuery(id+"F0.wireOp",EDGE,"E20.3.0.1"),sQuery(id+"F0.wireOp",EDGE,"E20.3.0.2"),sQuery(id+"F0.wireOp",EDGE,"E20.3.0.3"),sQuery(id+"F0.wireOp",EDGE,"E20.3.0.4"),sQuery(id+"F0.wireOp",EDGE,"E20.3.0.5"),sQuery(id+"F0.wireOp",EDGE,"E20.3.0.6"),sQuery(id+"F0.wireOp",EDGE,"E20.4.0.0"),sQuery(id+"F0.wireOp",EDGE,"E20.4.0.1"),sQuery(id+"F0.wireOp",EDGE,"E20.4.0.2"),sQuery(id+"F0.wireOp",EDGE,"E20.4.0.3"),sQuery(id+"F0.wireOp",EDGE,"E20.4.0.4"),sQuery(id+"F0.wireOp",EDGE,"E20.4.0.5"),sQuery(id+"F0.wireOp",EDGE,"E20.4.0.6"),sQuery(id+"F0.wireOp",EDGE,"E20.5.0.0"),sQuery(id+"F0.wireOp",EDGE,"E20.5.0.1"),sQuery(id+"F0.wireOp",EDGE,"E20.5.0.2"),sQuery(id+"F0.wireOp",EDGE,"E20.5.0.3"),sQuery(id+"F0.wireOp",EDGE,"E20.5.0.4"),sQuery(id+"F0.wireOp",EDGE,"E20.5.0.5"),sQuery(id+"F0.wireOp",EDGE,"E20.5.0.6"),sQuery(id+"F0.wireOp",EDGE,"E20.6.0.0"),sQuery(id+"F0.wireOp",EDGE,"E20.6.0.1"),sQuery(id+"F0.wireOp",EDGE,"E20.6.0.2"),sQuery(id+"F0.wireOp",EDGE,"E20.6.0.3"),sQuery(id+"F0.wireOp",EDGE,"E20.6.0.4"),sQuery(id+"F0.wireOp",EDGE,"E20.6.0.5"),sQuery(id+"F0.wireOp",EDGE,"E20.6.0.6"),sQuery(id+"F0.wireOp",EDGE,"E20.7.0.0"),sQuery(id+"F0.wireOp",EDGE,"E20.7.0.1"),sQuery(id+"F0.wireOp",EDGE,"E20.7.0.2"),sQuery(id+"F0.wireOp",EDGE,"E20.7.0.3"),sQuery(id+"F0.wireOp",EDGE,"E20.7.0.4"),sQuery(id+"F0.wireOp",EDGE,"E20.7.0.5"),sQuery(id+"F0.wireOp",EDGE,"E20.7.0.6"),sQuery(id+"F0.wireOp",EDGE,"E20.8.0.0"),sQuery(id+"F0.wireOp",EDGE,"E20.8.0.1"),sQuery(id+"F0.wireOp",EDGE,"E20.8.0.2"),sQuery(id+"F0.wireOp",EDGE,"E20.8.0.3"),sQuery(id+"F0.wireOp",EDGE,"E20.8.0.4"),sQuery(id+"F0.wireOp",EDGE,"E20.8.0.5"),sQuery(id+"F0.wireOp",EDGE,"E20.8.0.6"),sQuery(id+"F0.wireOp",EDGE,"E20.9.0.0"),sQuery(id+"F0.wireOp",EDGE,"E20.9.0.1"),sQuery(id+"F0.wireOp",EDGE,"E20.9.0.2"),sQuery(id+"F0.wireOp",EDGE,"E20.9.0.3"),sQuery(id+"F0.wireOp",EDGE,"E20.9.0.4"),sQuery(id+"F0.wireOp",EDGE,"E20.9.0.5"),sQuery(id+"F0.wireOp",EDGE,"E20.9.0.6"),sQuery(id+"F0.wireOp",EDGE,"E21.1.0.0"),sQuery(id+"F0.wireOp",EDGE,"E21.1.0.1"),sQuery(id+"F0.wireOp",EDGE,"E21.1.0.2"),sQuery(id+"F0.wireOp",EDGE,"E21.1.0.3"),sQuery(id+"F0.wireOp",EDGE,"E21.1.0.4"),sQuery(id+"F0.wireOp",EDGE,"E21.1.0.5"),sQuery(id+"F0.wireOp",EDGE,"E22.1.0.0"),sQuery(id+"F0.wireOp",EDGE,"E23.0.1.0"),sQuery(id+"F0.wireOp",EDGE,"E23.0.1.1"),sQuery(id+"F0.wireOp",EDGE,"E23.0.1.2"),sQuery(id+"F0.wireOp",EDGE,"E23.0.1.3"),sQuery(id+"F0.wireOp",EDGE,"E23.0.1.4"),sQuery(id+"F0.wireOp",EDGE,"E23.0.1.5"),sQuery(id+"F0.wireOp",EDGE,"E23.0.1.6"),sQuery(id+"F0.wireOp",EDGE,"E24.1.0.0"),sQuery(id+"F0.wireOp",EDGE,"E24.1.0.1"),sQuery(id+"F0.wireOp",EDGE,"E24.1.0.2"),sQuery(id+"F0.wireOp",EDGE,"E24.1.0.3"),sQuery(id+"F0.wireOp",EDGE,"E24.1.0.4"),sQuery(id+"F0.wireOp",EDGE,"E24.1.0.5"),sQuery(id+"F0.wireOp",EDGE,"E24.1.0.6"),sQuery(id+"F0.wireOp",EDGE,"E24.2.0.0"),sQuery(id+"F0.wireOp",EDGE,"E24.2.0.1"),sQuery(id+"F0.wireOp",EDGE,"E24.2.0.2"),sQuery(id+"F0.wireOp",EDGE,"E24.2.0.3"),sQuery(id+"F0.wireOp",EDGE,"E24.2.0.4"),sQuery(id+"F0.wireOp",EDGE,"E24.2.0.5"),sQuery(id+"F0.wireOp",EDGE,"E24.2.0.6"),sQuery(id+"F0.wireOp",EDGE,"E24.3.0.0"),sQuery(id+"F0.wireOp",EDGE,"E24.3.0.1"),sQuery(id+"F0.wireOp",EDGE,"E24.3.0.2"),sQuery(id+"F0.wireOp",EDGE,"E24.3.0.3"),sQuery(id+"F0.wireOp",EDGE,"E24.3.0.4"),sQuery(id+"F0.wireOp",EDGE,"E24.3.0.5"),sQuery(id+"F0.wireOp",EDGE,"E24.3.0.6"),sQuery(id+"F0.wireOp",EDGE,"E25.1.0.0"),sQuery(id+"F0.wireOp",EDGE,"E25.1.0.1"),sQuery(id+"F0.wireOp",EDGE,"E25.1.0.2"),sQuery(id+"F0.wireOp",EDGE,"E25.1.0.3"),sQuery(id+"F0.wireOp",EDGE,"E25.1.0.4"),sQuery(id+"F0.wireOp",EDGE,"E25.1.0.5"),sQuery(id+"F0.wireOp",EDGE,"E25.1.0.6"),sQuery(id+"F0.wireOp",EDGE,"E26"),sQuery(id+"F0.wireOp",EDGE,"E27"),sQuery(id+"F0.wireOp",EDGE,"E28"),sQuery(id+"F0.wireOp",EDGE,"E29"),sQuery(id+"F0.wireOp",EDGE,"E30"),sQuery(id+"F0.wireOp",EDGE,"E31"),sQuery(id+"F0.wireOp",EDGE,"E32"),sQuery(id+"F0.wireOp",EDGE,"E33")])],"isStart":true});
            extrude(context, id + "F3", {"entities" : qUnion([Q0, Q1]), "operationType" : NewBodyOperationType.ADD, "endBound" : BoundingType.UP_TO_SURFACE, "oppositeDirection" : true, "endBoundEntityFace" : qUnion([Q2]), "depth" : 25 * mm});
        }
    });
